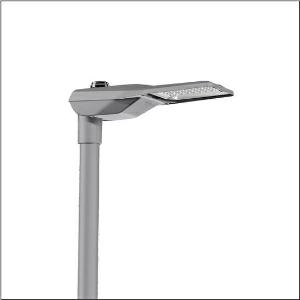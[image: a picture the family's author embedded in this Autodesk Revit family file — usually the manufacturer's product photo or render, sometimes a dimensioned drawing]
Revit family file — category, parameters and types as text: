
# Revit family: streetlight_sl_21_mini___st0_8a_5xe6c47n08hb_c463
name_source: partatom
category: Lighting Fixtures
units: mm (PartAtom-declared; Revit-internal decimal feet)

## family parameters
Cut with Voids When Loaded = No
Host = Face
Light Source = No
Part Type = Normal
Room Calculation Point = No
Round Connector Dimension = Use Diameter
Shared = No

## types (1)
- --- (1 x LED, 9430 lm, 66 W, 4000K)
    Apparent Load = 66 VA
    CIE Flux Codes = 38 75 97 100 100
    Color Rendering = 70
    Color Temperature = 4000K
    Default Elevation = 1800 mm
    Description = Streetlight SL 21 mini, mast luminaire, primary light control with lens, of PMMA, primary optical cover: cover, of toughened safety glass, transparent, light distribution: ST0.8a, light emission: direct distribution, primary light characteristic: asymmetric, installation type: side-entry, LED, 3G 1.5mm², High Power LED, rated luminous flux: 9.430lm, luminous efficacy: 143lm/W, light colour: 740, colour temperature: 4000K, control: overheat protection, pre-setting: linear dimming characteristic, constant luminous flux control, time-dependent luminous flux control, flexible luminous flux parameterisation, mains connection: 230..240V, AC, 50/60Hz, connection cable pre-assembled, cable length: 8,5m, wiring characteristics: H07RN-F, start of lifetime: 66W, end of service life: 69W, reduction: 30W, luminaire housing, of diecast aluminium (EN AC-44300), powder-coated, Siteco® metallic grey (DB 702S), corrosivity category C5 mid according to DIN EN ISO 12944, multi-level sealing system, sealing non-destructively replaceable, inclination adjustable: 0°, 5°, 10°, 15°, length: 628mm, width: 235mm, height: 110mm, spigot size: 42mm (side-entry), protection rating (complete): IP66, insulation class (complete): insulation class I (protective earthing), certification: CE, ENEC, ENEC+, VDE, impact resistance: IK09, permissible operating ambient temperature for outdoor applications: -40..+50°C, standard-compliant lighting for roads and squares, packaging unit: 1 piece

Light Distribution: ST0.8a
    Height = 110 mm
    Lamp = 1 x LED
    Lamp Light Flux = 9430 lm
    Lamp Power = 66 W
    Lamp count = 1
    Length = 625 mm
    Luminous efficacy = 143 lm/W
    Manufacturer = Siteco
    ModVariant = No
    Model = 5XE6C47N08HB
    Number of Poles = 1
    OnlyDefault = Yes
    Power Factor = 1
    Product Name = Streetlight SL 21 mini | ST0.8a
    Product group = mast luminaire | pylon top
    ProductGroupID = 6100
    Protection Class = Protection class I
    Protection Degree = IP 66
    RLX_Detail_Level = 1
    RLX_Emergency_Light_Flux = 0 lm
    RLX_Emergency_Type = 0
    RLX_Emergency_Type_DB = No
    RlxData = <blob elided: 92069 chars, md5=686f2511>
    Socket = socket
    Standby Power = 0 W
    System Light Flux = 9430 lm
    System Power = 66 W
    Type Comments = factory setting: luminous flux: 100 % | dim-lin: 254 | 670 mA
    Type Image = l_1294379.jpg
    URL = http://relux.com
    VarID = @adj_103951
    Voltage = 0 V
    Weight = 0.00 kg
    Width = 234 mm

## geometry (parser evidence)
native form markers: Blend x4, Sweep x13
no freeform markers — native parametric forms only
